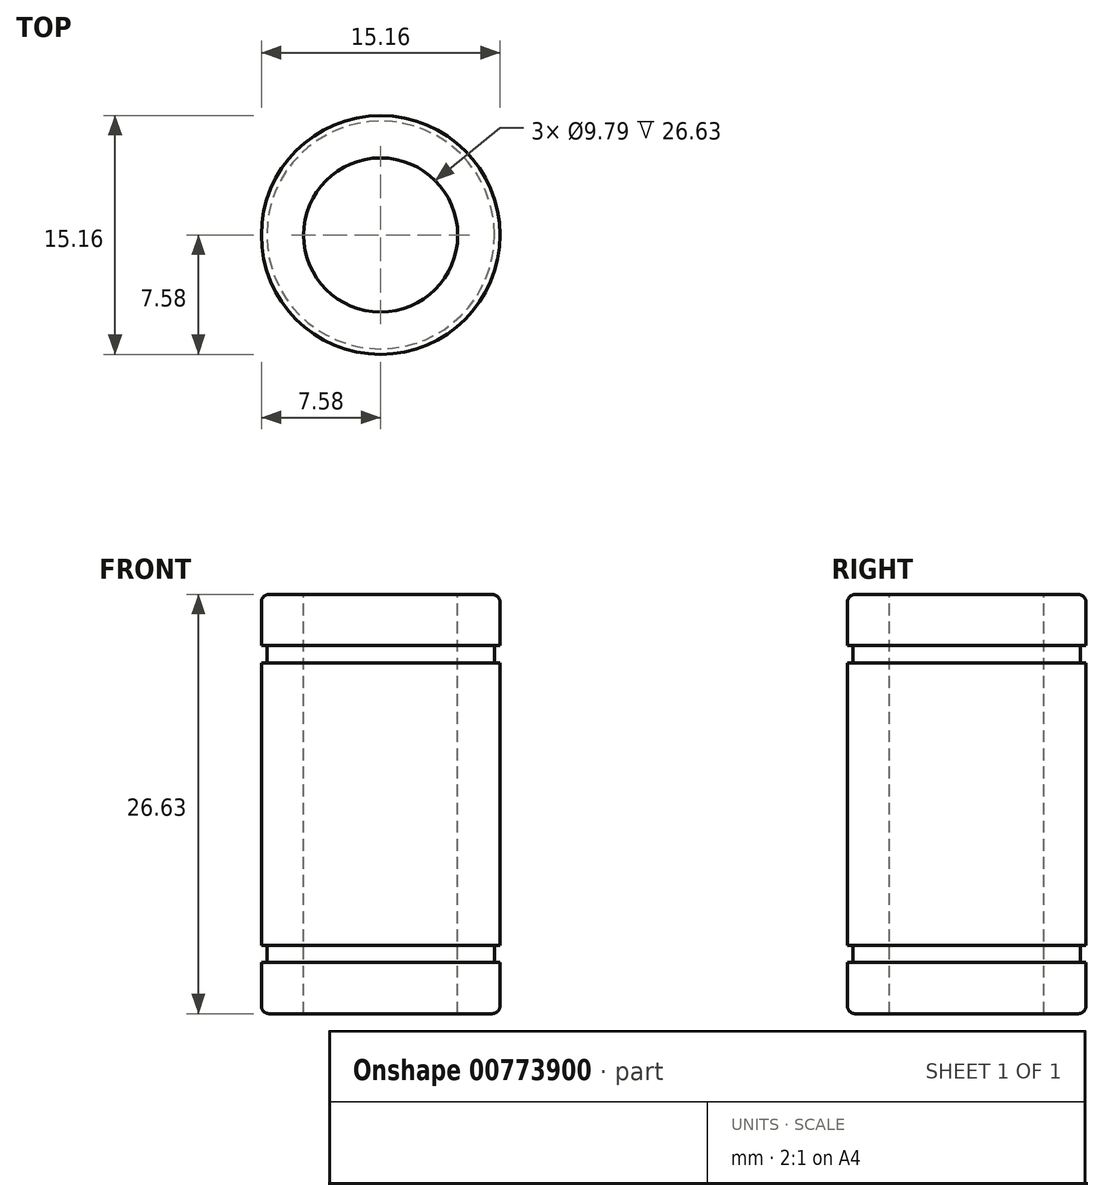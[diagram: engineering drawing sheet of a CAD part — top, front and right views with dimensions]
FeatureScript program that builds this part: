
annotation { "Feature Type Name" : "Feature", "Feature Type Description" : "" }
export const myFeature = defineFeature(function(context is Context, id is Id, definition is map)
    precondition{}
    {
        {
            var Q0;
            Q0=qCreatedBy(makeId("Front.planeOp"),FACE);
            var sketch = newSketch(context, id + "F0", { "sketchPlane" : qUnion([Q0])});
            skLineSegment(sketch, "E0", {"start": v(0, 0) * mm, "end": v(0, 26.63) * mm});
            skLineSegment(sketch, "E1", {"start": v(0, 26.63) * mm, "end": v(-7.58, 26.63) * mm});
            skLineSegment(sketch, "E2", {"start": v(-7.58, 26.63) * mm, "end": v(-7.58, 23.38) * mm});
            skLineSegment(sketch, "E3", {"start": v(-7.58, 23.38) * mm, "end": v(-7.23, 23.38) * mm});
            skLineSegment(sketch, "E4", {"start": v(-7.23, 23.38) * mm, "end": v(-7.23, 22.28) * mm});
            skLineSegment(sketch, "E5", {"start": v(-7.23, 22.28) * mm, "end": v(-7.58, 22.28) * mm});
            skLineSegment(sketch, "E6", {"start": v(-7.58, 3.25) * mm, "end": v(-7.23, 3.25) * mm});
            skLineSegment(sketch, "E7", {"start": v(-7.23, 4.35) * mm, "end": v(-7.23, 3.25) * mm});
            skLineSegment(sketch, "E8", {"start": v(-7.23, 4.35) * mm, "end": v(-7.58, 4.35) * mm});
            skLineSegment(sketch, "E9", {"start": v(-7.58, 0) * mm, "end": v(0, 0) * mm});
            skLineSegment(sketch, "E10", {"start": v(-7.58, 3.25) * mm, "end": v(-7.58, 0) * mm});
            skLineSegment(sketch, "E11", {"start": v(-7.58, 22.28) * mm, "end": v(-7.58, 4.35) * mm});
            skSolve(sketch);
        }
        {
            var Q0;
            Q0=makeQuery(id+"F0.imprint","IMPRINT",FACE,{"disambiguationData":[TD([[makeQuery(id+"F0.imprint","IMPRINT",EDGE,{"derivedFrom":sQuery(id+"F0.wireOp",EDGE,"E0")}),1.0]])]});
            var Q1;
            Q1=sQuery(id+"F0.wireOp",EDGE,"E0");
            revolve(context, id + "F1", {"entities" : qUnion([Q0]), "axis" : qUnion([Q1]), "revolveType" : RevolveType.FULL});
        }
        {
            var Q0;
            Q0=makeQuery(id+"F1.opRevolve","SWEPT_FACE",FACE,{"disambiguationData":[OSD([sQuery(id+"F0.wireOp",EDGE,"E1")])]});
            var sketch = newSketch(context, id + "F2", { "sketchPlane" : qUnion([Q0])});
            skCircle(sketch, "E12", {"center": v(0, 0) * mm, "radius": 4.9 * mm});
            skSolve(sketch);
        }
        {
            var Q0;
            Q0=qSketchRegion(id+"F2",true);
            extrude(context, id + "F3", {"entities" : qUnion([Q0]), "operationType" : NewBodyOperationType.REMOVE, "endBound" : BoundingType.THROUGH_ALL, "oppositeDirection" : true, "depth" : 25 * mm, "offsetDistance" : 25 * mm});
        }
        {
            var Q0;
            Q0=makeQuery(id+"F1.opRevolve","SWEPT_EDGE",EDGE,{"disambiguationData":[OSD([sQuery(id+"F0.wireOp",EDGE,"E9"),sQuery(id+"F0.wireOp",EDGE,"E10")])]});
            var Q1;
            Q1=makeQuery(id+"F1.opRevolve","SWEPT_EDGE",EDGE,{"disambiguationData":[OSD([sQuery(id+"F0.wireOp",EDGE,"E1"),sQuery(id+"F0.wireOp",EDGE,"E2")])]});
            fillet(context, id + "F4", {"entities" : qUnion([Q0, Q1]), "radius" : .5 * mm, "tangentPropagation" : true, "allowEdgeOverflow" : false});
        }
    });
